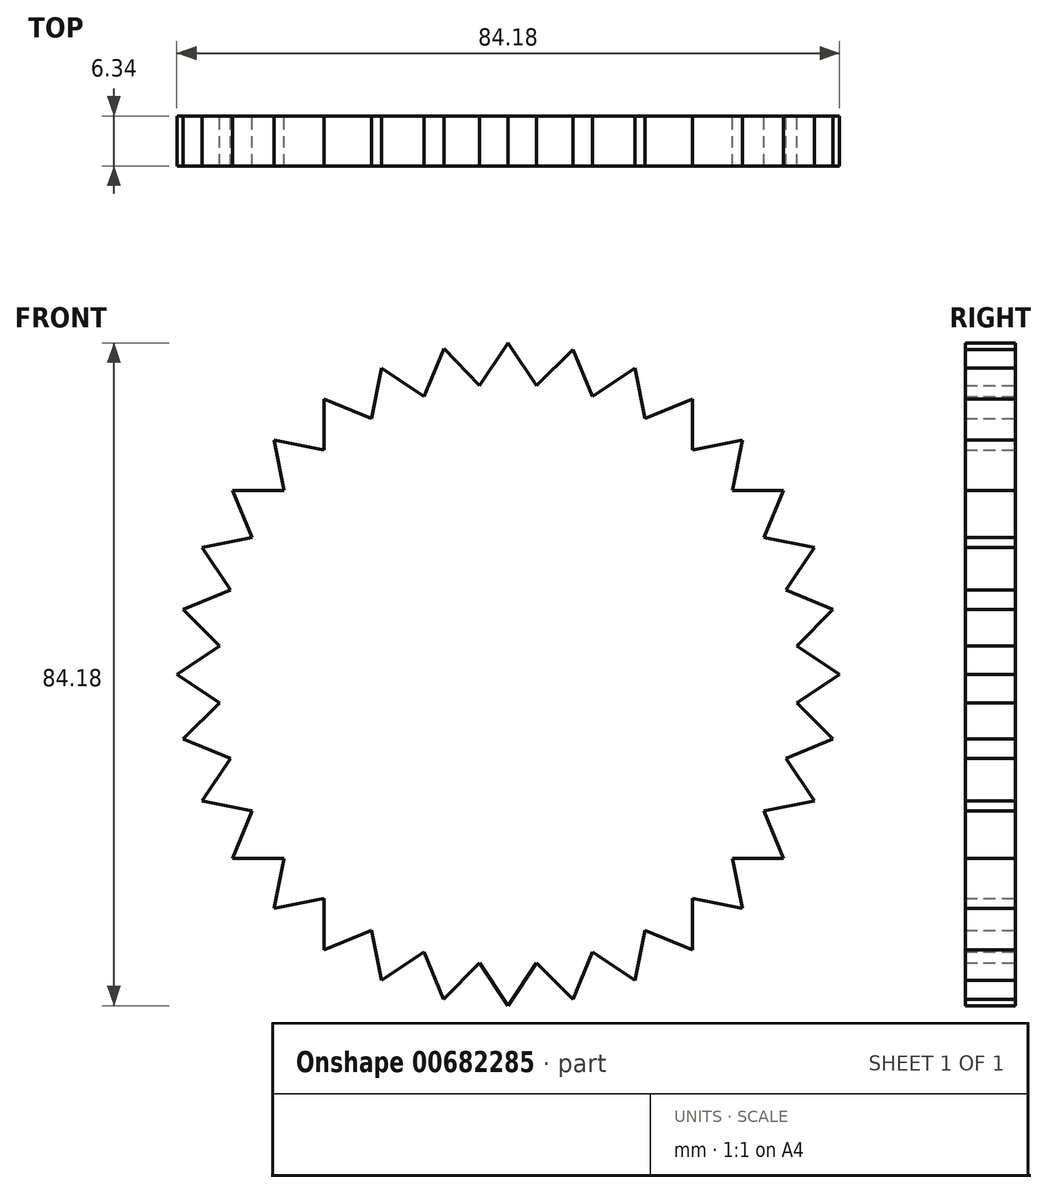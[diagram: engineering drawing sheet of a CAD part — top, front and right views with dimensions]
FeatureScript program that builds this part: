
annotation { "Feature Type Name" : "Feature", "Feature Type Description" : "" }
export const myFeature = defineFeature(function(context is Context, id is Id, definition is map)
    precondition{}
    {
        {
            var Q0;
            Q0=qCreatedBy(makeId("Front.planeOp"),FACE);
            var sketch = newSketch(context, id + "F0", { "sketchPlane" : qUnion([Q0])});
            skCircle(sketch, "E0.cCircle", {"center": v(0, 0) * mm, "radius": 36.68 * mm, "construction": true});
            skLineSegment(sketch, "E0.0", {"start": v(-23.38, 28.5) * mm, "end": v(-17.37, 32.5) * mm});
            skLineSegment(sketch, "E0.1", {"start": v(-17.37, 32.5) * mm, "end": v(-10.7, 35.27) * mm});
            skLineSegment(sketch, "E0.2", {"start": v(-10.7, 35.27) * mm, "end": v(-3.61, 36.68) * mm});
            skLineSegment(sketch, "E0.3", {"start": v(-3.61, 36.68) * mm, "end": v(3.61, 36.68) * mm});
            skLineSegment(sketch, "E0.4", {"start": v(3.61, 36.68) * mm, "end": v(10.7, 35.27) * mm});
            skLineSegment(sketch, "E0.5", {"start": v(10.7, 35.27) * mm, "end": v(17.37, 32.5) * mm});
            skLineSegment(sketch, "E0.6", {"start": v(17.37, 32.5) * mm, "end": v(23.38, 28.5) * mm});
            skLineSegment(sketch, "E0.7", {"start": v(23.38, 28.5) * mm, "end": v(28.5, 23.38) * mm});
            skLineSegment(sketch, "E0.8", {"start": v(28.5, 23.38) * mm, "end": v(32.5, 17.37) * mm});
            skLineSegment(sketch, "E0.9", {"start": v(32.5, 17.37) * mm, "end": v(35.27, 10.7) * mm});
            skLineSegment(sketch, "E0.10", {"start": v(35.27, 10.7) * mm, "end": v(36.68, 3.61) * mm});
            skLineSegment(sketch, "E0.11", {"start": v(36.68, 3.61) * mm, "end": v(36.68, -3.61) * mm});
            skLineSegment(sketch, "E0.12", {"start": v(36.68, -3.61) * mm, "end": v(35.27, -10.7) * mm});
            skLineSegment(sketch, "E0.13", {"start": v(35.27, -10.7) * mm, "end": v(32.5, -17.37) * mm});
            skLineSegment(sketch, "E0.14", {"start": v(32.5, -17.37) * mm, "end": v(28.5, -23.38) * mm});
            skLineSegment(sketch, "E0.15", {"start": v(28.5, -23.38) * mm, "end": v(23.38, -28.5) * mm});
            skLineSegment(sketch, "E0.16", {"start": v(23.38, -28.5) * mm, "end": v(17.37, -32.5) * mm});
            skLineSegment(sketch, "E0.17", {"start": v(17.37, -32.5) * mm, "end": v(10.7, -35.27) * mm});
            skLineSegment(sketch, "E0.18", {"start": v(10.7, -35.27) * mm, "end": v(3.61, -36.68) * mm});
            skLineSegment(sketch, "E0.19", {"start": v(3.61, -36.68) * mm, "end": v(-3.61, -36.68) * mm});
            skLineSegment(sketch, "E0.20", {"start": v(-3.61, -36.68) * mm, "end": v(-10.7, -35.27) * mm});
            skLineSegment(sketch, "E0.21", {"start": v(-10.7, -35.27) * mm, "end": v(-17.37, -32.5) * mm});
            skLineSegment(sketch, "E0.22", {"start": v(-17.37, -32.5) * mm, "end": v(-23.38, -28.5) * mm});
            skLineSegment(sketch, "E0.23", {"start": v(-23.38, -28.5) * mm, "end": v(-28.5, -23.38) * mm});
            skLineSegment(sketch, "E0.24", {"start": v(-28.5, -23.38) * mm, "end": v(-32.5, -17.37) * mm});
            skLineSegment(sketch, "E0.25", {"start": v(-32.5, -17.37) * mm, "end": v(-35.27, -10.7) * mm});
            skLineSegment(sketch, "E0.26", {"start": v(-35.27, -10.7) * mm, "end": v(-36.68, -3.61) * mm});
            skLineSegment(sketch, "E0.27", {"start": v(-36.68, -3.61) * mm, "end": v(-36.68, 3.61) * mm});
            skLineSegment(sketch, "E0.28", {"start": v(-36.68, 3.61) * mm, "end": v(-35.27, 10.7) * mm});
            skLineSegment(sketch, "E0.29", {"start": v(-35.27, 10.7) * mm, "end": v(-32.5, 17.37) * mm});
            skLineSegment(sketch, "E0.30", {"start": v(-32.5, 17.37) * mm, "end": v(-28.5, 23.38) * mm});
            skLineSegment(sketch, "E0.31", {"start": v(-28.5, 23.38) * mm, "end": v(-23.38, 28.5) * mm});
            skPoint(sketch, "E0.0.midPoint", {"position": v(-20.38, 30.5) * mm});
            skPoint(sketch, "E1.endSnap0", {"position": v(0, 36.68) * mm});
            skLineSegment(sketch, "E2", {"start": v(-3.61, 36.68) * mm, "end": v(0, 42.09) * mm});
            skLineSegment(sketch, "E3", {"start": v(0, 42.09) * mm, "end": v(3.61, 36.68) * mm});
            skLineSegment(sketch, "E4", {"start": v(3.61, 36.68) * mm, "end": v(-3.61, 36.68) * mm});
            skLineSegment(sketch, "E5", {"start": v(-10.7, 35.27) * mm, "end": v(-8.12, 41.36) * mm});
            skLineSegment(sketch, "E6", {"start": v(-8.12, 41.36) * mm, "end": v(-3.61, 36.68) * mm});
            skLineSegment(sketch, "E7", {"start": v(-17.37, 32.5) * mm, "end": v(-16.1, 38.88) * mm});
            skLineSegment(sketch, "E8", {"start": v(-16.1, 38.88) * mm, "end": v(-10.7, 35.27) * mm});
            skLineSegment(sketch, "E9", {"start": v(-17.37, 32.5) * mm, "end": v(-23.38, 35) * mm});
            skLineSegment(sketch, "E10", {"start": v(-23.38, 35) * mm, "end": v(-23.38, 28.5) * mm});
            skLineSegment(sketch, "E11", {"start": v(-28.5, 23.38) * mm, "end": v(-29.76, 29.76) * mm});
            skLineSegment(sketch, "E12", {"start": v(-29.76, 29.76) * mm, "end": v(-23.38, 28.5) * mm});
            skLineSegment(sketch, "E13", {"start": v(-28.5, 23.38) * mm, "end": v(-35, 23.38) * mm});
            skLineSegment(sketch, "E14", {"start": v(-35, 23.38) * mm, "end": v(-32.5, 17.37) * mm});
            skLineSegment(sketch, "E15", {"start": v(-32.5, 17.37) * mm, "end": v(-38.88, 16.1) * mm});
            skLineSegment(sketch, "E16", {"start": v(-38.88, 16.1) * mm, "end": v(-35.27, 10.7) * mm});
            skLineSegment(sketch, "E17", {"start": v(-35.27, 10.7) * mm, "end": v(-41.28, 8.21) * mm});
            skLineSegment(sketch, "E18", {"start": v(-41.28, 8.21) * mm, "end": v(-36.68, 3.61) * mm});
            skLineSegment(sketch, "E19", {"start": v(-36.68, 3.61) * mm, "end": v(-42.09, 0) * mm});
            skLineSegment(sketch, "E20", {"start": v(-42.09, 0) * mm, "end": v(-36.68, -3.61) * mm});
            skLineSegment(sketch, "E21", {"start": v(-36.68, -3.61) * mm, "end": v(-41.28, -8.21) * mm});
            skLineSegment(sketch, "E22", {"start": v(-41.28, -8.21) * mm, "end": v(-35.27, -10.7) * mm});
            skLineSegment(sketch, "E23", {"start": v(-35.27, -10.7) * mm, "end": v(-38.88, -16.1) * mm});
            skLineSegment(sketch, "E24", {"start": v(-38.88, -16.1) * mm, "end": v(-32.5, -17.37) * mm});
            skLineSegment(sketch, "E25", {"start": v(-32.5, -17.37) * mm, "end": v(-35, -23.38) * mm});
            skLineSegment(sketch, "E26", {"start": v(-35, -23.38) * mm, "end": v(-28.5, -23.38) * mm});
            skLineSegment(sketch, "E27", {"start": v(3.61, 36.68) * mm, "end": v(8.21, 41.28) * mm});
            skLineSegment(sketch, "E28", {"start": v(8.21, 41.28) * mm, "end": v(10.7, 35.27) * mm});
            skLineSegment(sketch, "E29", {"start": v(10.7, 35.27) * mm, "end": v(16.1, 38.88) * mm});
            skLineSegment(sketch, "E30", {"start": v(16.1, 38.88) * mm, "end": v(17.37, 32.5) * mm});
            skLineSegment(sketch, "E31", {"start": v(17.37, 32.5) * mm, "end": v(23.38, 35) * mm});
            skLineSegment(sketch, "E32", {"start": v(23.38, 35) * mm, "end": v(23.38, 28.5) * mm});
            skLineSegment(sketch, "E33", {"start": v(23.38, 28.5) * mm, "end": v(29.76, 29.76) * mm});
            skLineSegment(sketch, "E34", {"start": v(29.76, 29.76) * mm, "end": v(28.5, 23.38) * mm});
            skLineSegment(sketch, "E35", {"start": v(28.5, 23.38) * mm, "end": v(35, 23.38) * mm});
            skLineSegment(sketch, "E36", {"start": v(35, 23.38) * mm, "end": v(32.5, 17.37) * mm});
            skLineSegment(sketch, "E37", {"start": v(32.5, 17.37) * mm, "end": v(38.88, 16.1) * mm});
            skLineSegment(sketch, "E38", {"start": v(38.88, 16.1) * mm, "end": v(35.27, 10.7) * mm});
            skLineSegment(sketch, "E39", {"start": v(35.27, 10.7) * mm, "end": v(41.28, 8.21) * mm});
            skLineSegment(sketch, "E40", {"start": v(41.28, 8.21) * mm, "end": v(36.68, 3.61) * mm});
            skLineSegment(sketch, "E41", {"start": v(36.68, 3.61) * mm, "end": v(42.09, 0) * mm});
            skLineSegment(sketch, "E42", {"start": v(42.09, 0) * mm, "end": v(36.68, -3.61) * mm});
            skLineSegment(sketch, "E43", {"start": v(35.27, -10.7) * mm, "end": v(41.28, -8.21) * mm});
            skLineSegment(sketch, "E44", {"start": v(41.28, -8.21) * mm, "end": v(36.68, -3.61) * mm});
            skLineSegment(sketch, "E45", {"start": v(32.5, -17.37) * mm, "end": v(38.88, -16.1) * mm});
            skLineSegment(sketch, "E46", {"start": v(38.88, -16.1) * mm, "end": v(35.27, -10.7) * mm});
            skLineSegment(sketch, "E47", {"start": v(28.5, -23.38) * mm, "end": v(35, -23.38) * mm});
            skLineSegment(sketch, "E48", {"start": v(35, -23.38) * mm, "end": v(32.5, -17.37) * mm});
            skLineSegment(sketch, "E49", {"start": v(-28.5, -23.38) * mm, "end": v(-29.76, -29.76) * mm});
            skLineSegment(sketch, "E50", {"start": v(-29.76, -29.76) * mm, "end": v(-23.38, -28.5) * mm});
            skLineSegment(sketch, "E51", {"start": v(-23.38, -28.5) * mm, "end": v(-23.38, -35) * mm});
            skLineSegment(sketch, "E52", {"start": v(-23.38, -35) * mm, "end": v(-17.37, -32.5) * mm});
            skLineSegment(sketch, "E53", {"start": v(-17.37, -32.5) * mm, "end": v(-16.1, -38.88) * mm});
            skLineSegment(sketch, "E54", {"start": v(-16.1, -38.88) * mm, "end": v(-10.7, -35.27) * mm});
            skLineSegment(sketch, "E55", {"start": v(-10.7, -35.27) * mm, "end": v(-8.21, -41.28) * mm});
            skLineSegment(sketch, "E56", {"start": v(-8.21, -41.28) * mm, "end": v(-3.61, -36.68) * mm});
            skLineSegment(sketch, "E57", {"start": v(-3.61, -36.68) * mm, "end": v(0, -42.09) * mm});
            skLineSegment(sketch, "E58", {"start": v(0, -42.09) * mm, "end": v(3.61, -36.68) * mm});
            skLineSegment(sketch, "E59", {"start": v(3.61, -36.68) * mm, "end": v(8.21, -41.28) * mm});
            skLineSegment(sketch, "E60", {"start": v(8.21, -41.28) * mm, "end": v(10.7, -35.27) * mm});
            skLineSegment(sketch, "E61", {"start": v(17.37, -32.5) * mm, "end": v(23.38, -35) * mm});
            skLineSegment(sketch, "E62", {"start": v(23.38, -35) * mm, "end": v(23.38, -28.5) * mm});
            skLineSegment(sketch, "E63", {"start": v(23.38, -28.5) * mm, "end": v(29.76, -29.76) * mm});
            skLineSegment(sketch, "E64", {"start": v(29.76, -29.76) * mm, "end": v(28.5, -23.38) * mm});
            skLineSegment(sketch, "E65", {"start": v(10.7, -35.27) * mm, "end": v(16.1, -38.88) * mm});
            skLineSegment(sketch, "E66", {"start": v(16.1, -38.88) * mm, "end": v(17.37, -32.5) * mm});
            skSolve(sketch);
        }
        {
            var Q0;
            Q0 = qSketchRegion(id + "F0", true);
            extrude(context, id + "F1", {"entities" : qUnion([Q0]), "endBound" : BoundingType.SYMMETRIC, "depth" : 6.35 * mm, "offsetDistance" : 25.4 * mm});
        }
    });
